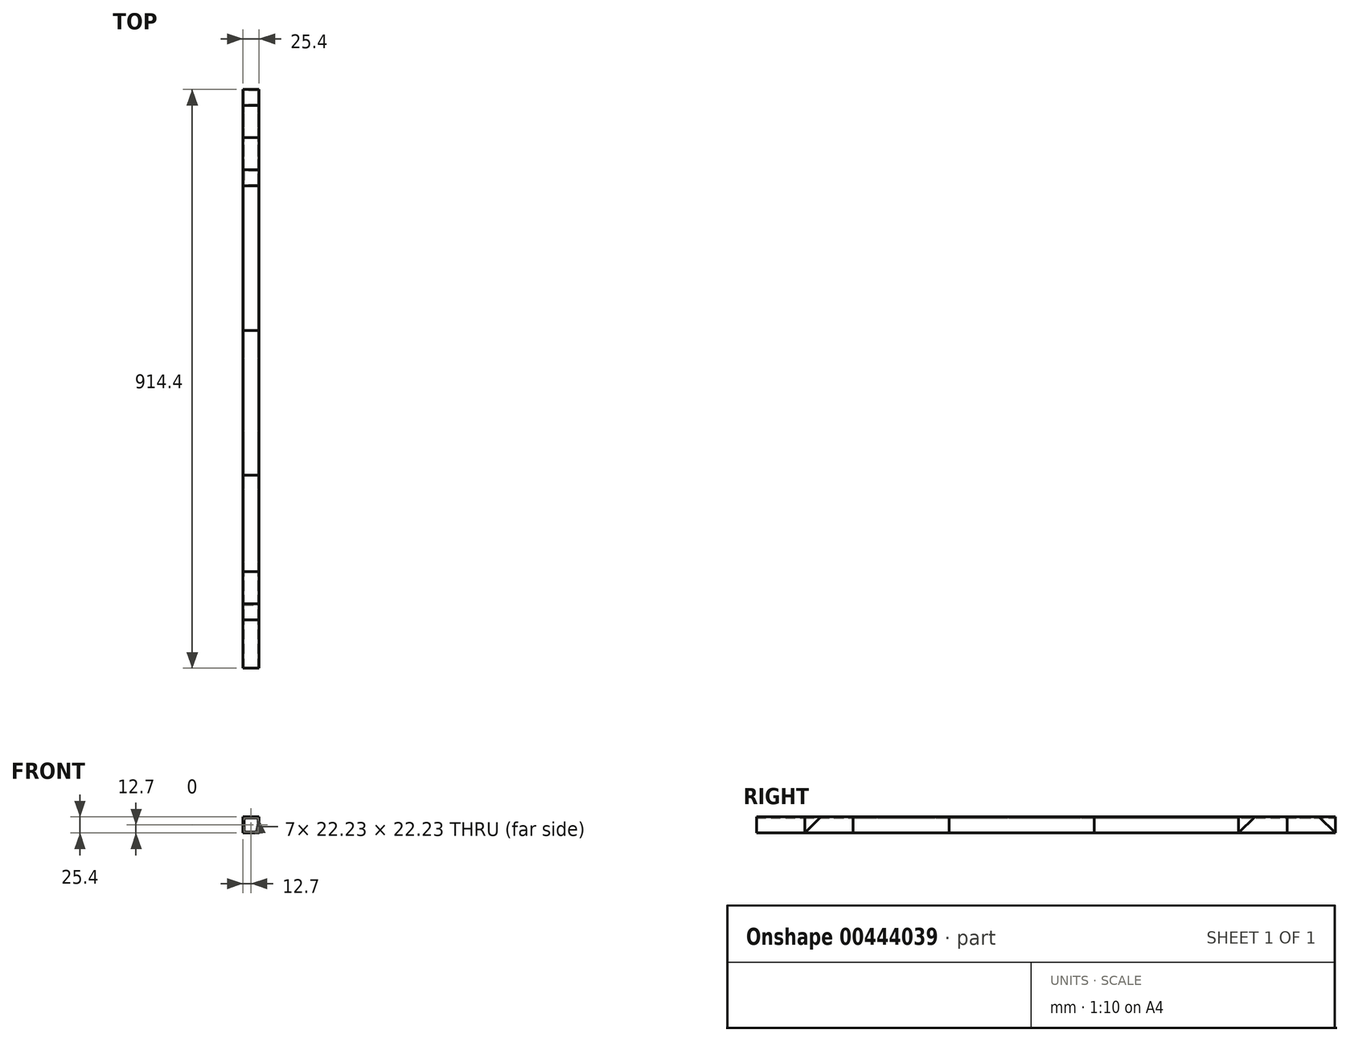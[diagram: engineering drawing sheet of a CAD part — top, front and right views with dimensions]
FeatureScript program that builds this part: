
annotation { "Feature Type Name" : "Feature", "Feature Type Description" : "" }
export const myFeature = defineFeature(function(context is Context, id is Id, definition is map)
    precondition{}
    {
        {
            var Q0;
            Q0=qCreatedBy(makeId("Front.planeOp"),FACE);
            var sketch = newSketch(context, id + "F0", { "sketchPlane" : qUnion([Q0])});
            skLineSegment(sketch, "E0.bottom", {"start": v(0, 0) * mm, "end": v(25.4, 0) * mm});
            skLineSegment(sketch, "E0.top", {"start": v(0, 25.4) * mm, "end": v(25.4, 25.4) * mm});
            skLineSegment(sketch, "E0.left", {"start": v(0, 0) * mm, "end": v(0, 25.4) * mm});
            skLineSegment(sketch, "E0.right", {"start": v(25.4, 0) * mm, "end": v(25.4, 25.4) * mm});
            skLineSegment(sketch, "E1.bottom", {"start": v(1.59, 1.59) * mm, "end": v(23.81, 1.59) * mm});
            skLineSegment(sketch, "E1.top", {"start": v(1.59, 23.81) * mm, "end": v(23.81, 23.81) * mm});
            skLineSegment(sketch, "E1.left", {"start": v(1.59, 1.59) * mm, "end": v(1.59, 23.81) * mm});
            skLineSegment(sketch, "E1.right", {"start": v(23.81, 1.59) * mm, "end": v(23.81, 23.81) * mm});
            skSolve(sketch);
        }
        {
            var Q0;
            Q0=makeQuery(id+"F0.imprint","IMPRINT",FACE,{"disambiguationData":[TD([[makeQuery(id+"F0.imprint","IMPRINT",EDGE,{"derivedFrom":sQuery(id+"F0.wireOp",EDGE,"E0.bottom")}),1.0]])]});
            extrude(context, id + "F1", {"entities" : qUnion([Q0]), "depth" : 914.4 * mm});
        }
        {
            var Q0;
            Q0=qSketchRegion(id+"F0",true);
            extrude(context, id + "F2", {"entities" : qUnion([Q0]), "depth" : 152.4 * mm});
        }
        {
            var Q0;
            Q0=qSketchRegion(id+"F0",true);
            extrude(context, id + "F3", {"entities" : qUnion([Q0]), "depth" : 381 * mm});
        }
        {
            var Q0;
            Q0=qSketchRegion(id+"F0",true);
            extrude(context, id + "F4", {"entities" : qUnion([Q0]), "depth" : 381 * mm});
        }
        {
            var Q0;
            Q0=qSketchRegion(id+"F0",true);
            extrude(context, id + "F5", {"entities" : qUnion([Q0]), "depth" : 609.6 * mm});
        }
        {
            var Q0;
            Q0=qSketchRegion(id+"F0",true);
            extrude(context, id + "F6", {"entities" : qUnion([Q0]), "depth" : 838.2 * mm});
        }
        {
            var Q0;
            Q0=qSketchRegion(id+"F0",true);
            extrude(context, id + "F7", {"entities" : qUnion([Q0]), "depth" : 76.2 * mm});
        }
        {
            var Q0;
            Q0=qSketchRegion(id+"F0",true);
            extrude(context, id + "F8", {"entities" : qUnion([Q0]), "depth" : 762 * mm});
        }
        {
            var Q0;
            Q0=qSketchRegion(id+"F0",true);
            extrude(context, id + "F9", {"entities" : qUnion([Q0]), "depth" : 152.4 * mm});
        }
        {
            var Q0;
            Q0=makeQuery(id+"F9.opExtrude","SWEPT_FACE",FACE,{"disambiguationData":[OSD([sQuery(id+"F0.wireOp",EDGE,"E0.right")])]});
            var sketch = newSketch(context, id + "F10", { "sketchPlane" : qUnion([Q0])});
            skLineSegment(sketch, "E2", {"start": v(-152.4, 0) * mm, "end": v(-127, 25.4) * mm});
            skLineSegment(sketch, "E3", {"start": v(0, 0) * mm, "end": v(-25.4, 25.4) * mm});
            skLineSegment(sketch, "E4", {"start": v(-127, 25.4) * mm, "end": v(-152.4, 25.4) * mm});
            skLineSegment(sketch, "E5", {"start": v(-152.4, 0) * mm, "end": v(-152.4, 25.4) * mm});
            skLineSegment(sketch, "E6", {"start": v(-25.4, 25.4) * mm, "end": v(0, 25.4) * mm});
            skSolve(sketch);
        }
        {
            var Q0;
            Q0=makeQuery(id+"F10.imprint","IMPRINT",FACE,{"disambiguationData":[TD([[makeQuery(id+"F10.imprint","IMPRINT",EDGE,{"derivedFrom":sQuery(id+"F10.wireOp",EDGE,"E2")}),1.0]])]});
            var Q1;
            Q1=makeQuery(id+"F10.imprint","IMPRINT",FACE,{"disambiguationData":[TD([[makeQuery(id+"F10.imprint","IMPRINT",EDGE,{"derivedFrom":sQuery(id+"F10.wireOp",EDGE,"E3")}),-1.0]])]});
            extrude(context, id + "F11", {"entities" : qUnion([Q0, Q1]), "operationType" : NewBodyOperationType.REMOVE, "oppositeDirection" : true, "depth" : 25.4 * mm});
        }
        {
            var Q0;
            Q0=makeQuery(id+"F6.opExtrude","SWEPT_FACE",FACE,{"disambiguationData":[OSD([sQuery(id+"F0.wireOp",EDGE,"E0.right")])]});
            var sketch = newSketch(context, id + "F12", { "sketchPlane" : qUnion([Q0])});
            skLineSegment(sketch, "E7", {"start": v(-838.2, 0) * mm, "end": v(-838.2, 25.4) * mm});
            skLineSegment(sketch, "E8", {"start": v(-838.2, 25.4) * mm, "end": v(-812.8, 25.4) * mm});
            skLineSegment(sketch, "E9", {"start": v(-812.8, 25.4) * mm, "end": v(-838.2, 0) * mm});
            skLineSegment(sketch, "E10", {"start": v(0, 0) * mm, "end": v(0, 25.4) * mm});
            skLineSegment(sketch, "E11", {"start": v(0, 25.4) * mm, "end": v(-25.4, 25.4) * mm});
            skLineSegment(sketch, "E12", {"start": v(-25.4, 25.4) * mm, "end": v(0, 0) * mm});
            skSolve(sketch);
        }
        {
            var Q0;
            Q0=makeQuery(id+"F12.imprint","IMPRINT",FACE,{"disambiguationData":[TD([[makeQuery(id+"F12.imprint","IMPRINT",EDGE,{"derivedFrom":sQuery(id+"F12.wireOp",EDGE,"E10")}),1.0]])]});
            var Q1;
            Q1=makeQuery(id+"F12.imprint","IMPRINT",FACE,{"disambiguationData":[TD([[makeQuery(id+"F12.imprint","IMPRINT",EDGE,{"derivedFrom":sQuery(id+"F12.wireOp",EDGE,"E7")}),-1.0]])]});
            extrude(context, id + "F13", {"entities" : qUnion([Q0, Q1]), "operationType" : NewBodyOperationType.REMOVE, "oppositeDirection" : true, "depth" : 25.4 * mm});
        }
        {
            var Q0;
            Q0=qSketchRegion(id+"F0",true);
            extrude(context, id + "F14", {"entities" : qUnion([Q0]), "depth" : 838.2 * mm});
        }
    });
